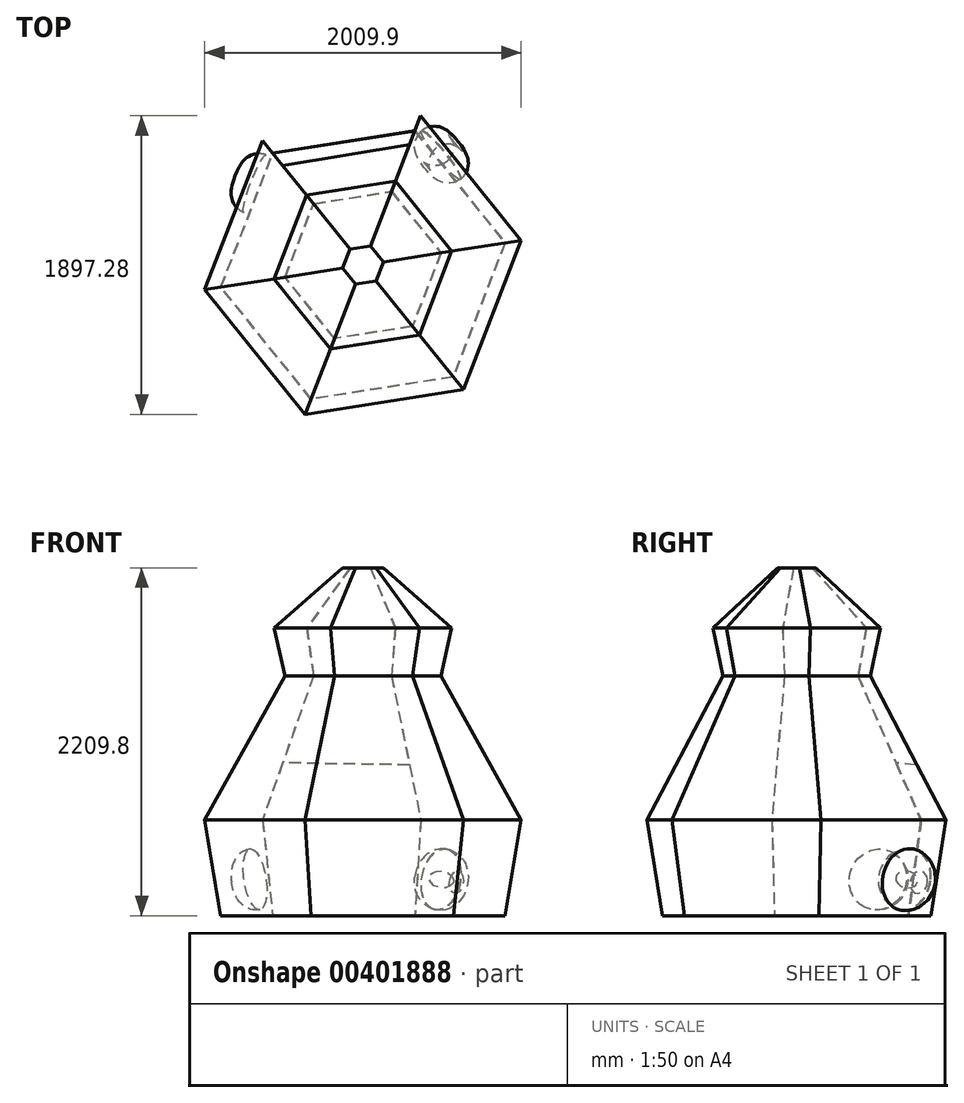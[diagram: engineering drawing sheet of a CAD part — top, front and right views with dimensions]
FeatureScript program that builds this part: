
annotation { "Feature Type Name" : "Feature", "Feature Type Description" : "" }
export const myFeature = defineFeature(function(context is Context, id is Id, definition is map)
    precondition{}
    {
        {
            var Q0;
            Q0=qCreatedBy(makeId("Top.planeOp"),FACE);
            var sketch = newSketch(context, id + "F0", { "sketchPlane" : qUnion([Q0])});
            skCircle(sketch, "E0.cCircle", {"center": v(0, 0) * mm, "radius": 791.9 * mm, "construction": true});
            skLineSegment(sketch, "E0.0", {"start": v(573.7, -712.03) * mm, "end": v(-329.78, -852.86) * mm});
            skLineSegment(sketch, "E0.1", {"start": v(-329.78, -852.86) * mm, "end": v(-903.49, -140.83) * mm});
            skLineSegment(sketch, "E0.2", {"start": v(-903.49, -140.83) * mm, "end": v(-573.7, 712.03) * mm});
            skLineSegment(sketch, "E0.3", {"start": v(-573.7, 712.03) * mm, "end": v(329.78, 852.86) * mm});
            skLineSegment(sketch, "E0.4", {"start": v(329.78, 852.86) * mm, "end": v(903.49, 140.83) * mm});
            skLineSegment(sketch, "E0.5", {"start": v(903.49, 140.83) * mm, "end": v(573.7, -712.03) * mm});
            skPoint(sketch, "E0.0.midPoint", {"position": v(121.96, -782.45) * mm});
            skSolve(sketch);
        }
        {
            var Q0;
            Q0 = qSketchRegion(id + "F0", true);
            extrude(context, id + "F1", {"entities" : qUnion([Q0]), "depth" : 609.6 * mm, "hasDraft" : true, "draftAngle" : 8.3 * degree});
        }
        {
            var Q0;
            Q0=makeQuery(id+"F1.opExtrude","CAP_FACE",FACE,{"disambiguationData":[OSD([sQuery(id+"F0.wireOp",EDGE,"E0.0"),sQuery(id+"F0.wireOp",EDGE,"E0.1"),sQuery(id+"F0.wireOp",EDGE,"E0.2"),sQuery(id+"F0.wireOp",EDGE,"E0.3"),sQuery(id+"F0.wireOp",EDGE,"E0.4"),sQuery(id+"F0.wireOp",EDGE,"E0.5")])],"isStart":false});
            var sketch = newSketch(context, id + "F2", { "sketchPlane" : qUnion([Q0])});
            skCircle(sketch, "E1.cCircle", {"center": v(0, 0) * mm, "radius": 880.82 * mm, "construction": true});
            skLineSegment(sketch, "E1.0", {"start": v(-366.82, -948.64) * mm, "end": v(-1004.95, -156.65) * mm});
            skLineSegment(sketch, "E1.1", {"start": v(-1004.95, -156.65) * mm, "end": v(-638.14, 792) * mm});
            skLineSegment(sketch, "E1.2", {"start": v(-638.14, 792) * mm, "end": v(366.82, 948.64) * mm});
            skLineSegment(sketch, "E1.3", {"start": v(366.82, 948.64) * mm, "end": v(1004.95, 156.65) * mm});
            skLineSegment(sketch, "E1.4", {"start": v(1004.95, 156.65) * mm, "end": v(638.14, -792) * mm});
            skLineSegment(sketch, "E1.5", {"start": v(638.14, -792) * mm, "end": v(-366.82, -948.64) * mm});
            skPoint(sketch, "E1.0.midPoint", {"position": v(-685.89, -552.64) * mm});
            skSolve(sketch);
        }
        {
            var Q0;
            Q0 = qSketchRegion(id + "F2", true);
            extrude(context, id + "F3", {"entities" : qUnion([Q0]), "operationType" : NewBodyOperationType.ADD, "depth" : 914.4 * mm, "hasDraft" : true, "draftAngle" : 26 * degree, "draftPullDirection" : true});
        }
        {
            var Q0;
            Q0=makeQuery(id+"F3.opExtrude","CAP_FACE",FACE,{"disambiguationData":[OSD([sQuery(id+"F2.wireOp",EDGE,"E1.0"),sQuery(id+"F2.wireOp",EDGE,"E1.1"),sQuery(id+"F2.wireOp",EDGE,"E1.2"),sQuery(id+"F2.wireOp",EDGE,"E1.3"),sQuery(id+"F2.wireOp",EDGE,"E1.4"),sQuery(id+"F2.wireOp",EDGE,"E1.5")])],"isStart":false});
            var sketch = newSketch(context, id + "F4", { "sketchPlane" : qUnion([Q0])});
            skCircle(sketch, "E2.cCircle", {"center": v(0, 0) * mm, "radius": 434.84 * mm, "construction": true});
            skLineSegment(sketch, "E2.0", {"start": v(315.03, -390.99) * mm, "end": v(-181.09, -468.32) * mm});
            skLineSegment(sketch, "E2.1", {"start": v(-181.09, -468.32) * mm, "end": v(-496.12, -77.33) * mm});
            skLineSegment(sketch, "E2.2", {"start": v(-496.12, -77.33) * mm, "end": v(-315.03, 390.99) * mm});
            skLineSegment(sketch, "E2.3", {"start": v(-315.03, 390.99) * mm, "end": v(181.09, 468.32) * mm});
            skLineSegment(sketch, "E2.4", {"start": v(181.09, 468.32) * mm, "end": v(496.12, 77.33) * mm});
            skLineSegment(sketch, "E2.5", {"start": v(496.12, 77.33) * mm, "end": v(315.03, -390.99) * mm});
            skPoint(sketch, "E2.0.midPoint", {"position": v(66.97, -429.65) * mm});
            skSolve(sketch);
        }
        {
            var Q0;
            Q0 = qSketchRegion(id + "F4", true);
            extrude(context, id + "F5", {"entities" : qUnion([Q0]), "operationType" : NewBodyOperationType.ADD, "depth" : 304.8 * mm, "hasDraft" : true, "draftAngle" : 11 * degree});
        }
        {
            var Q0;
            Q0=makeQuery(id+"F5.opExtrude","CAP_FACE",FACE,{"disambiguationData":[OSD([sQuery(id+"F4.wireOp",EDGE,"E2.0"),sQuery(id+"F4.wireOp",EDGE,"E2.1"),sQuery(id+"F4.wireOp",EDGE,"E2.2"),sQuery(id+"F4.wireOp",EDGE,"E2.3"),sQuery(id+"F4.wireOp",EDGE,"E2.4"),sQuery(id+"F4.wireOp",EDGE,"E2.5")])],"isStart":false});
            var sketch = newSketch(context, id + "F6", { "sketchPlane" : qUnion([Q0])});
            skCircle(sketch, "E3.cCircle", {"center": v(0, 0) * mm, "radius": 494.09 * mm, "construction": true});
            skLineSegment(sketch, "E3.0", {"start": v(357.96, -444.26) * mm, "end": v(-205.76, -532.13) * mm});
            skLineSegment(sketch, "E3.1", {"start": v(-205.76, -532.13) * mm, "end": v(-563.72, -87.87) * mm});
            skLineSegment(sketch, "E3.2", {"start": v(-563.72, -87.87) * mm, "end": v(-357.96, 444.26) * mm});
            skLineSegment(sketch, "E3.3", {"start": v(-357.96, 444.26) * mm, "end": v(205.76, 532.13) * mm});
            skLineSegment(sketch, "E3.4", {"start": v(205.76, 532.13) * mm, "end": v(563.72, 87.87) * mm});
            skLineSegment(sketch, "E3.5", {"start": v(563.72, 87.87) * mm, "end": v(357.96, -444.26) * mm});
            skPoint(sketch, "E3.0.midPoint", {"position": v(76.1, -488.2) * mm});
            skSolve(sketch);
        }
        {
            var Q0;
            Q0 = qSketchRegion(id + "F6", true);
            extrude(context, id + "F7", {"entities" : qUnion([Q0]), "operationType" : NewBodyOperationType.ADD, "depth" : 381 * mm, "hasDraft" : true, "draftAngle" : 45 * degree, "draftPullDirection" : true});
        }
        {
            var Q0;
            Q0=makeQuery(id+"F1.opExtrude","SWEPT_FACE",FACE,{"disambiguationData":[OSD([sQuery(id+"F0.wireOp",EDGE,"E0.4")])]});
            var sketch = newSketch(context, id + "F8", { "sketchPlane" : qUnion([Q0])});
            skCircle(sketch, "E4", {"center": v(271.6, 318.44) * mm, "radius": 197.7 * mm});
            skSolve(sketch);
        }
        {
            var Q0;
            Q0 = qSketchRegion(id + "F8", true);
            extrude(context, id + "F9", {"entities" : qUnion([Q0]), "operationType" : NewBodyOperationType.ADD, "depth" : 127 * mm});
        }
        {
            var Q0;
            Q0=makeQuery(id+"F9.opExtrude","CAP_EDGE",EDGE,{"disambiguationData":[OSD([sQuery(id+"F8.wireOp",EDGE,"E4")])],"isStart":false});
            fillet(context, id + "F10", {"entities" : qUnion([Q0]), "radius" : 127 * mm, "tangentPropagation" : true, "allowEdgeOverflow" : false});
        }
        {
            var Q0;
            Q0=makeQuery(id+"F1.opExtrude","CAP_FACE",FACE,{"disambiguationData":[OSD([sQuery(id+"F0.wireOp",EDGE,"E0.0"),sQuery(id+"F0.wireOp",EDGE,"E0.1"),sQuery(id+"F0.wireOp",EDGE,"E0.2"),sQuery(id+"F0.wireOp",EDGE,"E0.3"),sQuery(id+"F0.wireOp",EDGE,"E0.4"),sQuery(id+"F0.wireOp",EDGE,"E0.5")])],"isStart":true});
            shell(context, id + "F11", {"entities" : qUnion([Q0]), "thickness" : 2.54 * mm});
        }
        {
            var Q0;
            Q0=makeQuery(id+"F1.opExtrude","SWEPT_FACE",FACE,{"disambiguationData":[OSD([sQuery(id+"F0.wireOp",EDGE,"E0.3")])]});
            var sketch = newSketch(context, id + "F12", { "sketchPlane" : qUnion([Q0])});
            skLineSegment(sketch, "E5", {"start": v(-491.99, 741.62) * mm, "end": v(524.85, 718.74) * mm});
            skLineSegment(sketch, "E6", {"start": v(524.85, 718.74) * mm, "end": v(459.66, 104) * mm});
            skLineSegment(sketch, "E7", {"start": v(459.66, 104) * mm, "end": v(-454.51, 124.57) * mm});
            skLineSegment(sketch, "E8", {"start": v(-454.51, 124.57) * mm, "end": v(-491.99, 741.62) * mm});
            skSolve(sketch);
        }
        {
            var Q0;
            Q0 = qSketchRegion(id + "F12", true);
            extrude(context, id + "F13", {"entities" : qUnion([Q0]), "operationType" : NewBodyOperationType.REMOVE, "oppositeDirection" : true, "depth" : 25.4 * mm});
        }
        {
            var Q0;
            Q0=makeQuery(id+"F3.opExtrude","SWEPT_FACE",FACE,{"disambiguationData":[OSD([sQuery(id+"F2.wireOp",EDGE,"E1.2")])]});
            var sketch = newSketch(context, id + "F14", { "sketchPlane" : qUnion([Q0])});
            skLineSegment(sketch, "E9", {"start": v(-518.39, 126.73) * mm, "end": v(-446.72, 521.33) * mm});
            skLineSegment(sketch, "E10", {"start": v(-446.72, 521.33) * mm, "end": v(367.27, 590.64) * mm});
            skLineSegment(sketch, "E11", {"start": v(367.27, 590.64) * mm, "end": v(496.33, 196.07) * mm});
            skLineSegment(sketch, "E12", {"start": v(496.33, 196.07) * mm, "end": v(-518.39, 126.73) * mm});
            skSolve(sketch);
        }
        {
            var Q0;
            Q0=makeQuery(id+"F14.imprint","IMPRINT",FACE,{"disambiguationData":[TD([[makeQuery(id+"F14.imprint","IMPRINT",EDGE,{"derivedFrom":sQuery(id+"F14.wireOp",EDGE,"E9")}),1.0]])]});
            extrude(context, id + "F15", {"entities" : qUnion([Q0]), "operationType" : NewBodyOperationType.REMOVE, "oppositeDirection" : true, "depth" : 25.4 * mm});
        }
        {
            var Q0;
            Q0=makeQuery(id+"F1.opExtrude","SWEPT_FACE",FACE,{"disambiguationData":[OSD([sQuery(id+"F0.wireOp",EDGE,"E0.2")])]});
            var sketch = newSketch(context, id + "F16", { "sketchPlane" : qUnion([Q0])});
            skCircle(sketch, "E13", {"center": v(-254, 334.05) * mm, "radius": 195.14 * mm});
            skSolve(sketch);
        }
        {
            var Q0;
            Q0 = qSketchRegion(id + "F16", true);
            extrude(context, id + "F17", {"entities" : qUnion([Q0]), "operationType" : NewBodyOperationType.ADD, "depth" : 127 * mm});
        }
        {
            var Q0;
            Q0=makeQuery(id+"F17.opExtrude","CAP_EDGE",EDGE,{"disambiguationData":[OSD([sQuery(id+"F16.wireOp",EDGE,"E13")])],"isStart":false});
            fillet(context, id + "F18", {"entities" : qUnion([Q0]), "radius" : 127 * mm, "tangentPropagation" : true, "allowEdgeOverflow" : false});
        }
    });
